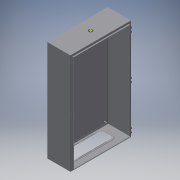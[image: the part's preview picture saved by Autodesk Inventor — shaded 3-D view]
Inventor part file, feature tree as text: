
AUTODESK INVENTOR PART (.ipt)
format: ipt  version: 2017 (Build 210142000, 142)  size: 1,804,800 bytes
history: native  units: in
note: dims shown in document units (in); Inventor stores cm internally (conversion verified against a paired STEP export)
features: other x1, hole x1, sketch x1
ambient origin geometry x8: Origin, YZ Plane, XZ Plane, XY Plane, X Axis, Y Axis, Z Axis, Center Point
bodies: Solid1 (feature_tree)
feature tree (3):
  other  "nsycrn106250t"
  hole  "Hole1"  [1 undecoded]
  sketch  "Sketch1"  dims[d0=0.3937in d1=0.3937in d2=1.5748in d3=0.2362in d4=0.1575in d5=0.0787in d6=90.0deg d7=0.315in d8=0.8108in]
note: 1 required parameter value undecoded (feature->parameter linkage not recoverable at this tier; creation-order binding heuristic only, values carry confidence <= 0.55)
